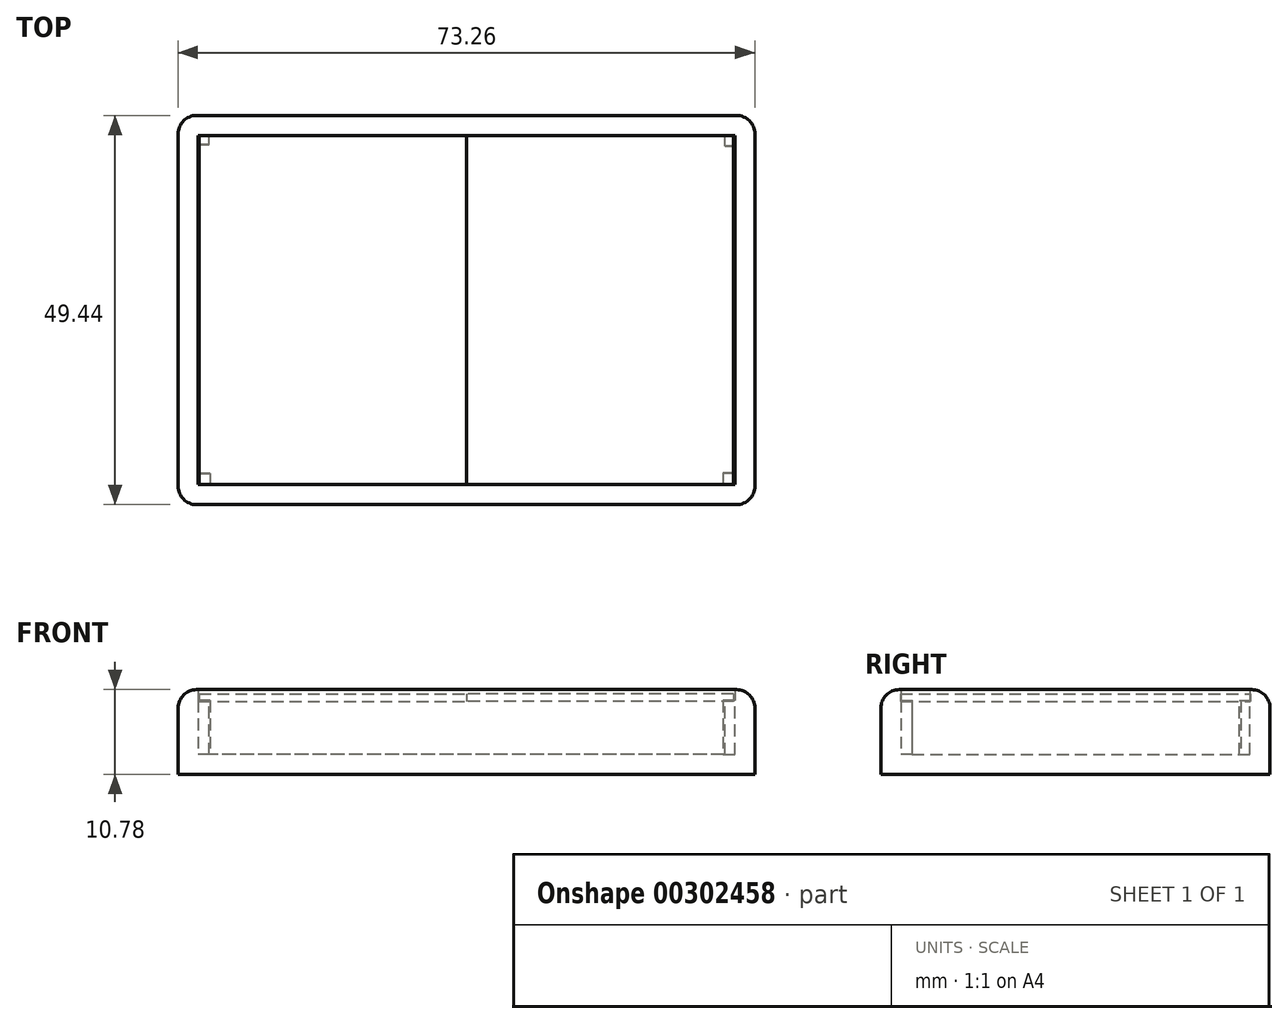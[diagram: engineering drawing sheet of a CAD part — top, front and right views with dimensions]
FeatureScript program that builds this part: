
annotation { "Feature Type Name" : "Feature", "Feature Type Description" : "" }
export const myFeature = defineFeature(function(context is Context, id is Id, definition is map)
    precondition{}
    {
        {
            var Q0;
            Q0=qCreatedBy(makeId("Top.planeOp"),FACE);
            var sketch = newSketch(context, id + "F0", { "sketchPlane" : qUnion([Q0])});
            skLineSegment(sketch, "E0.bottom", {"start": v(36.63, -24.72) * mm, "end": v(-36.63, -24.72) * mm});
            skLineSegment(sketch, "E0.top", {"start": v(36.63, 24.72) * mm, "end": v(-36.63, 24.72) * mm});
            skLineSegment(sketch, "E0.left", {"start": v(36.63, -24.72) * mm, "end": v(36.63, 24.72) * mm});
            skLineSegment(sketch, "E0.right", {"start": v(-36.63, -24.72) * mm, "end": v(-36.63, 24.72) * mm});
            skPoint(sketch, "E0.middle", {"position": v(0, 0) * mm});
            skSolve(sketch);
        }
        {
            var Q0;
            Q0 = qSketchRegion(id + "F0", true);
            extrude(context, id + "F1", {"entities" : qUnion([Q0]), "depth" : 10.78 * mm});
        }
        {
            var Q0;
            Q0=makeQuery(id+"F1.opExtrude","CAP_FACE",FACE,{"disambiguationData":[OSD([sQuery(id+"F0.wireOp",EDGE,"E0.bottom"),sQuery(id+"F0.wireOp",EDGE,"E0.top"),sQuery(id+"F0.wireOp",EDGE,"E0.left"),sQuery(id+"F0.wireOp",EDGE,"E0.right")])],"isStart":false});
            shell(context, id + "F2", {"entities" : qUnion([Q0]), "thickness" : 2.54 * mm});
        }
        {
            var Q0;
            Q0=makeQuery(id+"F1.opExtrude","CAP_EDGE",EDGE,{"disambiguationData":[OSD([sQuery(id+"F0.wireOp",EDGE,"E0.bottom")])],"isStart":false});
            var Q1;
            Q1=makeQuery(id+"F1.opExtrude","CAP_EDGE",EDGE,{"disambiguationData":[OSD([sQuery(id+"F0.wireOp",EDGE,"E0.left")])],"isStart":false});
            var Q2;
            Q2=makeQuery(id+"F1.opExtrude","CAP_EDGE",EDGE,{"disambiguationData":[OSD([sQuery(id+"F0.wireOp",EDGE,"E0.top")])],"isStart":false});
            var Q3;
            Q3=makeQuery(id+"F1.opExtrude","CAP_EDGE",EDGE,{"disambiguationData":[OSD([sQuery(id+"F0.wireOp",EDGE,"E0.right")])],"isStart":false});
            var Q4;
            Q4=makeQuery(id+"F1.opExtrude","SWEPT_EDGE",EDGE,{"disambiguationData":[OSD([sQuery(id+"F0.wireOp",EDGE,"E0.bottom"),sQuery(id+"F0.wireOp",EDGE,"E0.right")])]});
            var Q5;
            Q5=makeQuery(id+"F1.opExtrude","SWEPT_EDGE",EDGE,{"disambiguationData":[OSD([sQuery(id+"F0.wireOp",EDGE,"E0.bottom"),sQuery(id+"F0.wireOp",EDGE,"E0.left")])]});
            var Q6;
            Q6=makeQuery(id+"F1.opExtrude","SWEPT_EDGE",EDGE,{"disambiguationData":[OSD([sQuery(id+"F0.wireOp",EDGE,"E0.top"),sQuery(id+"F0.wireOp",EDGE,"E0.left")])]});
            var Q7;
            Q7=makeQuery(id+"F1.opExtrude","SWEPT_EDGE",EDGE,{"disambiguationData":[OSD([sQuery(id+"F0.wireOp",EDGE,"E0.top"),sQuery(id+"F0.wireOp",EDGE,"E0.right")])]});
            fillet(context, id + "F3", {"entities" : qUnion([Q0, Q1, Q2, Q3, Q4, Q5, Q6, Q7]), "radius" : 2.34 * mm, "tangentPropagation" : true, "allowEdgeOverflow" : false});
        }
        {
            var Q0;
            Q0=qCreatedBy(makeId("Top.planeOp"),FACE);
            var sketch = newSketch(context, id + "F4", { "sketchPlane" : qUnion([Q0])});
            skLineSegment(sketch, "E1.bottom", {"start": v(-34.1, 22.3) * mm, "end": v(-32.7, 22.3) * mm});
            skLineSegment(sketch, "E1.top", {"start": v(-34.1, 21) * mm, "end": v(-32.7, 21) * mm});
            skLineSegment(sketch, "E1.left", {"start": v(-34.1, 22.3) * mm, "end": v(-34.1, 21) * mm});
            skLineSegment(sketch, "E1.right", {"start": v(-32.7, 22.3) * mm, "end": v(-32.7, 21) * mm});
            skSolve(sketch);
        }
        {
            var Q0;
            Q0 = qSketchRegion(id + "F4", true);
            extrude(context, id + "F5", {"entities" : qUnion([Q0]), "operationType" : NewBodyOperationType.ADD, "depth" : 9.4 * mm});
        }
        {
            var Q0;
            Q0=qCreatedBy(makeId("Top.planeOp"),FACE);
            var sketch = newSketch(context, id + "F6", { "sketchPlane" : qUnion([Q0])});
            skLineSegment(sketch, "E2.bottom", {"start": v(-34.13, -22.26) * mm, "end": v(-32.57, -22.26) * mm});
            skLineSegment(sketch, "E2.top", {"start": v(-34.13, -20.75) * mm, "end": v(-32.57, -20.75) * mm});
            skLineSegment(sketch, "E2.left", {"start": v(-34.13, -22.26) * mm, "end": v(-34.13, -20.75) * mm});
            skLineSegment(sketch, "E2.right", {"start": v(-32.57, -22.26) * mm, "end": v(-32.57, -20.75) * mm});
            skSolve(sketch);
        }
        {
            var Q0;
            Q0 = qSketchRegion(id + "F6", true);
            extrude(context, id + "F7", {"entities" : qUnion([Q0]), "operationType" : NewBodyOperationType.ADD, "depth" : 9.4 * mm});
        }
        {
            var Q0;
            Q0=qCreatedBy(makeId("Top.planeOp"),FACE);
            var sketch = newSketch(context, id + "F8", { "sketchPlane" : qUnion([Q0])});
            skLineSegment(sketch, "E3.bottom", {"start": v(34.37, 22.26) * mm, "end": v(32.83, 22.26) * mm});
            skLineSegment(sketch, "E3.top", {"start": v(34.37, 20.8) * mm, "end": v(32.83, 20.8) * mm});
            skLineSegment(sketch, "E3.left", {"start": v(34.37, 22.26) * mm, "end": v(34.37, 20.8) * mm});
            skLineSegment(sketch, "E3.right", {"start": v(32.83, 22.26) * mm, "end": v(32.83, 20.8) * mm});
            skSolve(sketch);
        }
        {
            var Q0;
            Q0 = qSketchRegion(id + "F8", true);
            extrude(context, id + "F9", {"entities" : qUnion([Q0]), "operationType" : NewBodyOperationType.ADD, "depth" : 9.4 * mm});
        }
        {
            var Q0;
            Q0=qCreatedBy(makeId("Top.planeOp"),FACE);
            var sketch = newSketch(context, id + "F10", { "sketchPlane" : qUnion([Q0])});
            skLineSegment(sketch, "E4.bottom", {"start": v(34.21, -22.33) * mm, "end": v(32.55, -22.33) * mm});
            skLineSegment(sketch, "E4.top", {"start": v(34.21, -20.73) * mm, "end": v(32.55, -20.73) * mm});
            skLineSegment(sketch, "E4.left", {"start": v(34.21, -22.33) * mm, "end": v(34.21, -20.73) * mm});
            skLineSegment(sketch, "E4.right", {"start": v(32.55, -22.33) * mm, "end": v(32.55, -20.73) * mm});
            skSolve(sketch);
        }
        {
            var Q0;
            Q0 = qSketchRegion(id + "F10", true);
            extrude(context, id + "F11", {"entities" : qUnion([Q0]), "operationType" : NewBodyOperationType.ADD, "depth" : 9.4 * mm});
        }
        {
            var Q0;
            Q0=qCreatedBy(makeId("Right.planeOp"),FACE);
            var sketch = newSketch(context, id + "F12", { "sketchPlane" : qUnion([Q0])});
            skLineSegment(sketch, "E5.bottom", {"start": v(-22.2, 10.25) * mm, "end": v(22.2, 10.25) * mm});
            skLineSegment(sketch, "E5.top", {"start": v(-22.2, 9.25) * mm, "end": v(22.2, 9.25) * mm});
            skLineSegment(sketch, "E5.left", {"start": v(-22.2, 10.25) * mm, "end": v(-22.2, 9.25) * mm});
            skLineSegment(sketch, "E5.right", {"start": v(22.2, 10.25) * mm, "end": v(22.2, 9.25) * mm});
            skPoint(sketch, "E5.middle", {"position": v(0, 9.75) * mm});
            skSolve(sketch);
        }
        {
            var Q0;
            Q0 = qSketchRegion(id + "F12", true);
            extrude(context, id + "F13", {"entities" : qUnion([Q0]), "depth" : 33.9 * mm});
        }
        {
            var Q0;
            Q0=makeQuery(id+"F13.opExtrude","CAP_FACE",FACE,{"disambiguationData":[OSD([sQuery(id+"F12.wireOp",EDGE,"E5.bottom"),sQuery(id+"F12.wireOp",EDGE,"E5.top"),sQuery(id+"F12.wireOp",EDGE,"E5.left"),sQuery(id+"F12.wireOp",EDGE,"E5.right")])],"isStart":true});
            extrude(context, id + "F14", {"entities" : qUnion([Q0]), "depth" : 33.95 * mm});
        }
    });
